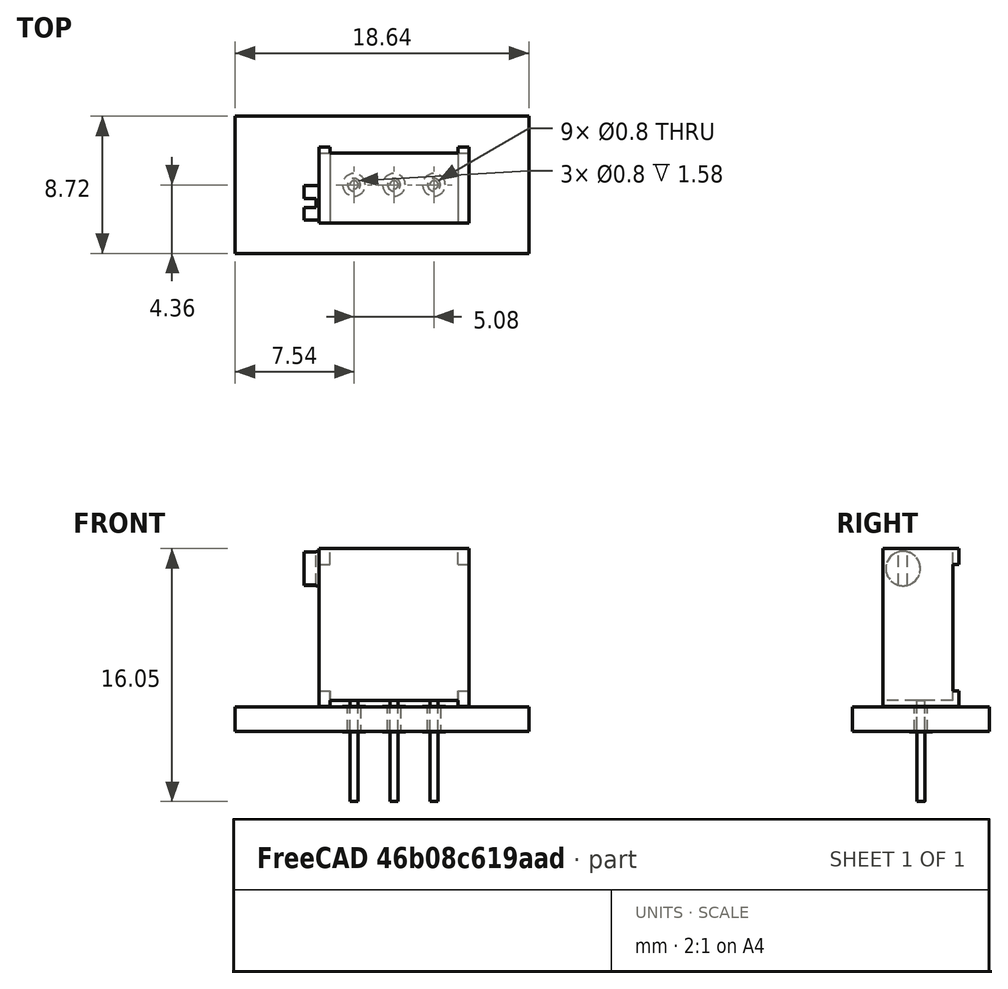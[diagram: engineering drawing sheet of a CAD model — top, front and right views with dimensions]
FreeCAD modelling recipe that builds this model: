
FCSTD DOCUMENT  (FreeCAD 0.18R15611 (Git))
Label: Potentiometer_Bourns_3296X_Horizontal
License: All rights reserved
LicenseURL: http://en.wikipedia.org/wiki/All_rights_reserved
objects: Part::FeaturePython×7, Part::Box×6, Part::Cylinder×4, Part::MultiFuse×2, App::DocumentObjectGroup×1, Part::Cut×1, Part::Feature×1
note: 21 computed .brp shape members not serialized (recipe doc carries the construction recipe); baked Part::Feature solids carry a one-line shape summary decoded from their .brp

FEATURE [Part::FeaturePython] FCrtYd_lines  label="FCrtYd"  # a2plus imported part (geometry in sourceFile) (typed FeaturePython)
  fixedPosition = true
FEATURE [Part::FeaturePython] FFab_lines  label="FFab"  # a2plus imported part (geometry in sourceFile) (typed FeaturePython)
  fixedPosition = true
FEATURE [Part::FeaturePython] Filk_lines  label="FrontSilk"  # a2plus imported part (geometry in sourceFile) (typed FeaturePython)
  fixedPosition = true
FEATURE [Part::FeaturePython] TopPads  # a2plus imported part (geometry in sourceFile) (typed FeaturePython)
  fixedPosition = true
FEATURE [Part::FeaturePython] BotPads  # a2plus imported part (geometry in sourceFile) (typed FeaturePython)
  fixedPosition = true
FEATURE [Part::FeaturePython] THPs  label="PTHs"  # a2plus imported part (geometry in sourceFile) (typed FeaturePython)
  fixedPosition = true
FEATURE [Part::FeaturePython] newPCB  label="Pcb"  # a2plus imported part (geometry in sourceFile) (typed FeaturePython)
  fixedPosition = true
FEATURE [App::DocumentObjectGroup] Potentiometer_Bourns_3296X_Horizontal_fp
  Group = -> [FCrtYd_lines,FFab_lines,Filk_lines,TopPads,BotPads,THPs,newPCB]
FEATURE [Part::Cylinder] Cylinder002  label="Pin2"
  Angle = 360
  AttacherType = Attacher::AttachEngine3D
  Height = 6.4
  Placement = pos=(-2.54,0,-6.02) rot=(0,0,1;0rad)
  Radius = 0.255
FEATURE [Part::Cylinder] Cylinder001  label="Pin3"
  Angle = 360
  AttacherType = Attacher::AttachEngine3D
  Height = 6.4
  Placement = pos=(-5.08,0,-6.02) rot=(0,0,1;0rad)
  Radius = 0.255
FEATURE [Part::Cylinder] Cylinder003  label="Knob"
  Angle = 360
  AttacherType = Attacher::AttachEngine3D
  Height = 1.02
  Placement = pos=(-0.405,-2.25,7.24) rot=(0,0,1;0rad)
  Radius = 1.095
FEATURE [Part::Box] Box003  label="Cube001"
  AttacherType = Attacher::AttachEngine3D
  Height = 0.76
  Length = 10
  Placement = pos=(-5,-2.54,7.5) rot=(0,0,1;0rad)
  Width = 0.56
FEATURE [Part::Cut] Cut  label="CutKnob"
  Base = -> Cylinder003
  Placement = pos=(0,1.11,9.17) rot=(0,-1,0;1.5708rad)
  Refine = true
  Tool = -> Box003
FEATURE [Part::Cylinder] Cylinder  label="Pin1"
  Angle = 360
  AttacherType = Attacher::AttachEngine3D
  Height = 6.4
  Placement = pos=(0,0,-6.02) rot=(0,0,1;0rad)
  Radius = 0.255
FEATURE [Part::Box] Box004  label="StandoffFront"
  AttacherType = Attacher::AttachEngine3D
  Height = 4.83
  Length = 1
  Width = 0.7
FEATURE [Part::Box] Box007  label="StandoffBack001"
  AttacherType = Attacher::AttachEngine3D
  Height = 4.83
  Length = 1
  Placement = pos=(9.03,8.83,0) rot=(0,0,1;0rad)
  Width = 0.7
FEATURE [Part::Box] Box005  label="StandoffBack"
  AttacherType = Attacher::AttachEngine3D
  Height = 4.83
  Length = 1
  Placement = pos=(9.03,0,0) rot=(0,0,1;0rad)
  Width = 0.7
FEATURE [Part::Box] Box  label="Body"
  AttacherType = Attacher::AttachEngine3D
  Height = 4.45
  Length = 9.65
  Placement = pos=(0,0,0.38) rot=(0,0,1;0rad)
  Width = 9.53
FEATURE [Part::Box] Box006  label="StandoffFront001"
  AttacherType = Attacher::AttachEngine3D
  Height = 4.83
  Length = 1
  Placement = pos=(0,8.83,0) rot=(0,0,1;0rad)
  Width = 0.7
FEATURE [Part::MultiFuse] Fusion  label="FusionBody"
  Placement = pos=(-7.305,2.41,10.03) rot=(0.57735,0.57735,-0.57735;2.0944rad)
  Refine = true
  Shapes = -> [Box,Box004,Box005,Box006,Box007]
FEATURE [Part::MultiFuse] FusionBody_mp_cp  label="FusionBody_fd"
  Refine = true
  Shapes = -> [Fusion,Cut,Cylinder002,Cylinder001,Cylinder]
FEATURE [Part::Feature] Shape  label="Potentiometer_Bourns_3296X_Horizontal"
  shape: bbox 10.49 x 4.83 x 16.05 mm, 32 faces (baked)
